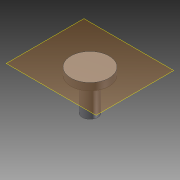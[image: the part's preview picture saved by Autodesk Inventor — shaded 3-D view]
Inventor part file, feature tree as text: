
AUTODESK INVENTOR PART (.ipt)
format: ipt  version: 2012 (Build 160160000, 160)  size: 80,384 bytes
history: native  units: mm
features: extrude x2, sketch x2, reference x2, plane x1, projected_geometry x1
ambient origin geometry x8: Origin, YZ Plane, XZ Plane, XY Plane, X Axis, Y Axis, Z Axis, Center Point
bodies: Solid1 (feature_tree)
feature tree (8):
  plane  "Work Plane1"
  extrude  "Extrusion1"  Depth=2.2mm TaperAngle=0.0deg
  extrude  "Extrusion2"  Depth=10.0mm TaperAngle=0.0deg
  sketch  "Sketch2"  dims[d0=0.3mm d1=2.2mm d2=0.0mm]
  reference  "Reference1"
  sketch  "Sketch3"  dims[d3=0.3mm d4=10.0mm d5=0.0mm]
  projected_geometry  "Projected Loop1"
  reference  "Reference2"
